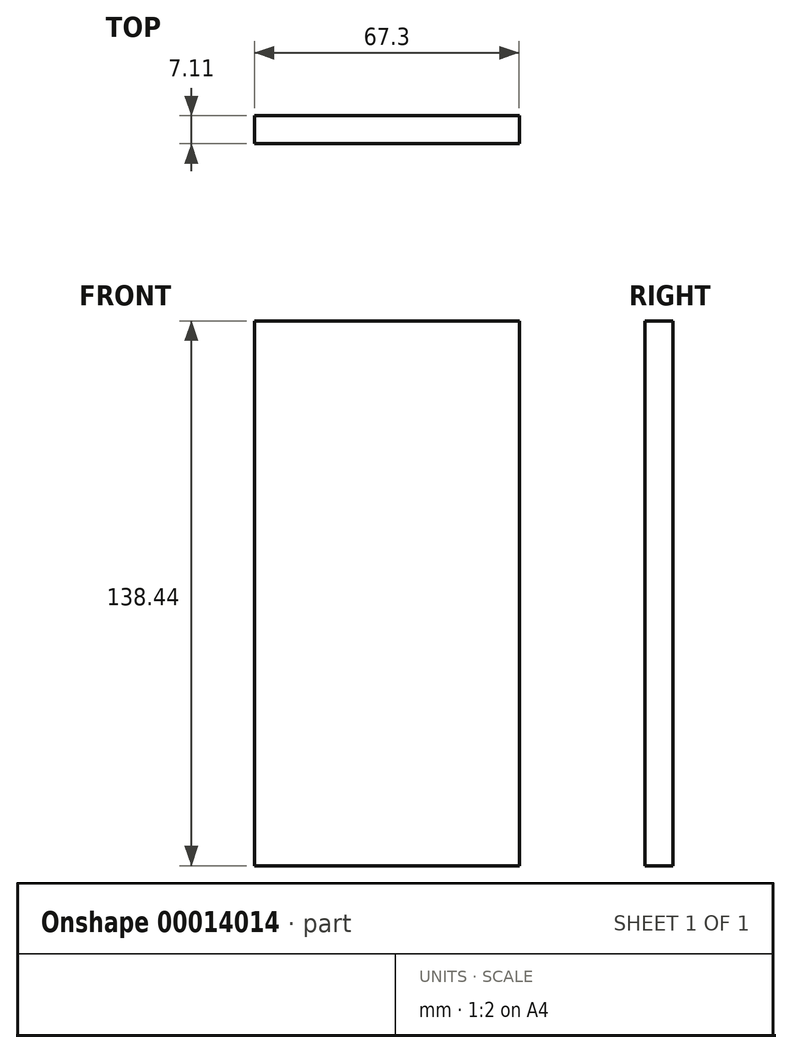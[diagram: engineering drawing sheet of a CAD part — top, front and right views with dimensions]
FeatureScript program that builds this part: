
annotation { "Feature Type Name" : "Feature", "Feature Type Description" : "" }
export const myFeature = defineFeature(function(context is Context, id is Id, definition is map)
    precondition{}
    {
        {
            var Q0;
            Q0=qCreatedBy(makeId("Front.planeOp"),FACE);
            var sketch = newSketch(context, id + "F0", { "sketchPlane" : qUnion([Q0])});
            skLineSegment(sketch, "E0.rect.bottom", {"start": v(33.65, -69.22) * mm, "end": v(-33.66, -69.22) * mm});
            skLineSegment(sketch, "E0.rect.top", {"start": v(33.65, 69.22) * mm, "end": v(-33.66, 69.22) * mm});
            skLineSegment(sketch, "E0.rect.left", {"start": v(33.65, -69.22) * mm, "end": v(33.65, 69.22) * mm});
            skLineSegment(sketch, "E0.rect.right", {"start": v(-33.66, -69.22) * mm, "end": v(-33.66, 69.22) * mm});
            skPoint(sketch, "E0.rect.middle", {"position": v(0, 0) * mm});
            skSolve(sketch);
        }
        {
            var Q0;
            Q0=makeQuery(id+"F0.imprint","IMPRINT",FACE,{"disambiguationData":[TD([[makeQuery(id+"F0.imprint","IMPRINT",EDGE,{"derivedFrom":sQuery(id+"F0.wireOp",EDGE,"E0.rect.bottom")}),-1.0]])]});
            extrude(context, id + "F1", {"entities" : qUnion([Q0]), "depth" : 7.11 * mm});
        }
    });
